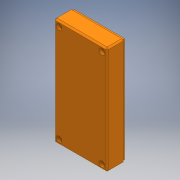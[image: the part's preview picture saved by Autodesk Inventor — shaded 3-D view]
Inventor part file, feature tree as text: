
AUTODESK INVENTOR PART (.ipt)
format: ipt  version: 2017.3 (Build 213256000, 256)  size: 282,624 bytes
history: native  units: mm
features: extrude x12, sketch x12, pattern_linear x1, chamfer x1
ambient origin geometry x8: Origin, YZ Plane, XZ Plane, XY Plane, X Axis, Y Axis, Z Axis, Center Point
bodies: Solid1 (feature_tree)
feature tree (26):
  extrude  "Extrusion1"  Depth=148.0mm
  extrude  "Extrusion2"  Depth=4.0mm
  extrude  "Extrusion3"  TaperAngle=90.0deg  [1 undecoded]
  extrude  "Extrusion4"  Depth=140.0mm
  extrude  "Extrusion5"  Depth=1.9mm
  extrude  "Extrusion6"  Depth=69.0mm
  pattern_linear  "Rectangular Pattern1"  Spacing1=3.0mm  [1 undecoded]
  extrude  "Extrusion7"  TaperAngle=180.0deg  [1 undecoded]
  extrude  "Extrusion8"  Depth=3.0mm
  extrude  "Extrusion9"  Depth=4.0mm
  extrude  "Extrusion10"  Depth=6.0mm TaperAngle=0.0deg
  extrude  "Extrusion11"  Depth=6.0mm
  extrude  "Extrusion12"  Depth=4.0mm TaperAngle=0.0deg
  chamfer  "Chamfer1"  Distance=59.0mm
  sketch  "Sketch1"  dims[d0=73.0mm d1=148.0mm]
  sketch  "Sketch2"  dims[d2=4.0mm d3=0.0mm d4=4.0mm]
  sketch  "Sketch3"  dims[d5=4.0mm d6=90.0deg]
  sketch  "Sketch4"  dims[d7=65.0mm d8=140.0mm]
  sketch  "Sketch5"  dims[d9=22.0mm d10=0.0mm d11=1.9mm]
  sketch  "Sketch6"  dims[d12=1.9mm d13=69.0mm]
  sketch  "Sketch7"  dims[d14=144.0mm]
  sketch  "Sketch8"  dims[d15=69.0mm]
  sketch  "Sketch9"  dims[d16=4.0mm d17=0.0mm]
  sketch  "Sketch10"  dims[d18=6.0mm]
  sketch  "Sketch11"  dims[d19=6.0mm]
  sketch  "Sketch12"  dims[d20=15.0mm d21=0.0mm d22=3.0mm d23=180.0deg d24=3.0mm d25=4.0mm d26=20.0mm d27=0.0mm d28=7.0mm d32=4.0mm d33=0.0mm d34=20.0mm d36=59.0mm d37=20.0mm d39=134.0mm d41=7.0mm d42=8.0mm d43=1.6mm d44=1.6mm d45=1.2mm d46=0.0mm d47=1.6mm d48=1.6mm d49=1.6mm d55=7.6mm d56=7.6mm d57=1.6mm d58=1.6mm d59=90.0deg d60=1.2mm d61=0.0mm d62=6.0mm d63=0.0mm d64=4.1mm d65=4.1mm d66=4.1mm d67=4.1mm d68=200.0mm d69=0.0mm d70=4.1mm d71=100.0mm d72=0.0mm d73=4.1mm d74=100.0mm d75=0.0mm d77=2.0mm d78=2.0mm d79=45.0deg]
note: 3 required parameter values undecoded (feature->parameter linkage not recoverable at this tier; creation-order binding heuristic only, values carry confidence <= 0.55)
